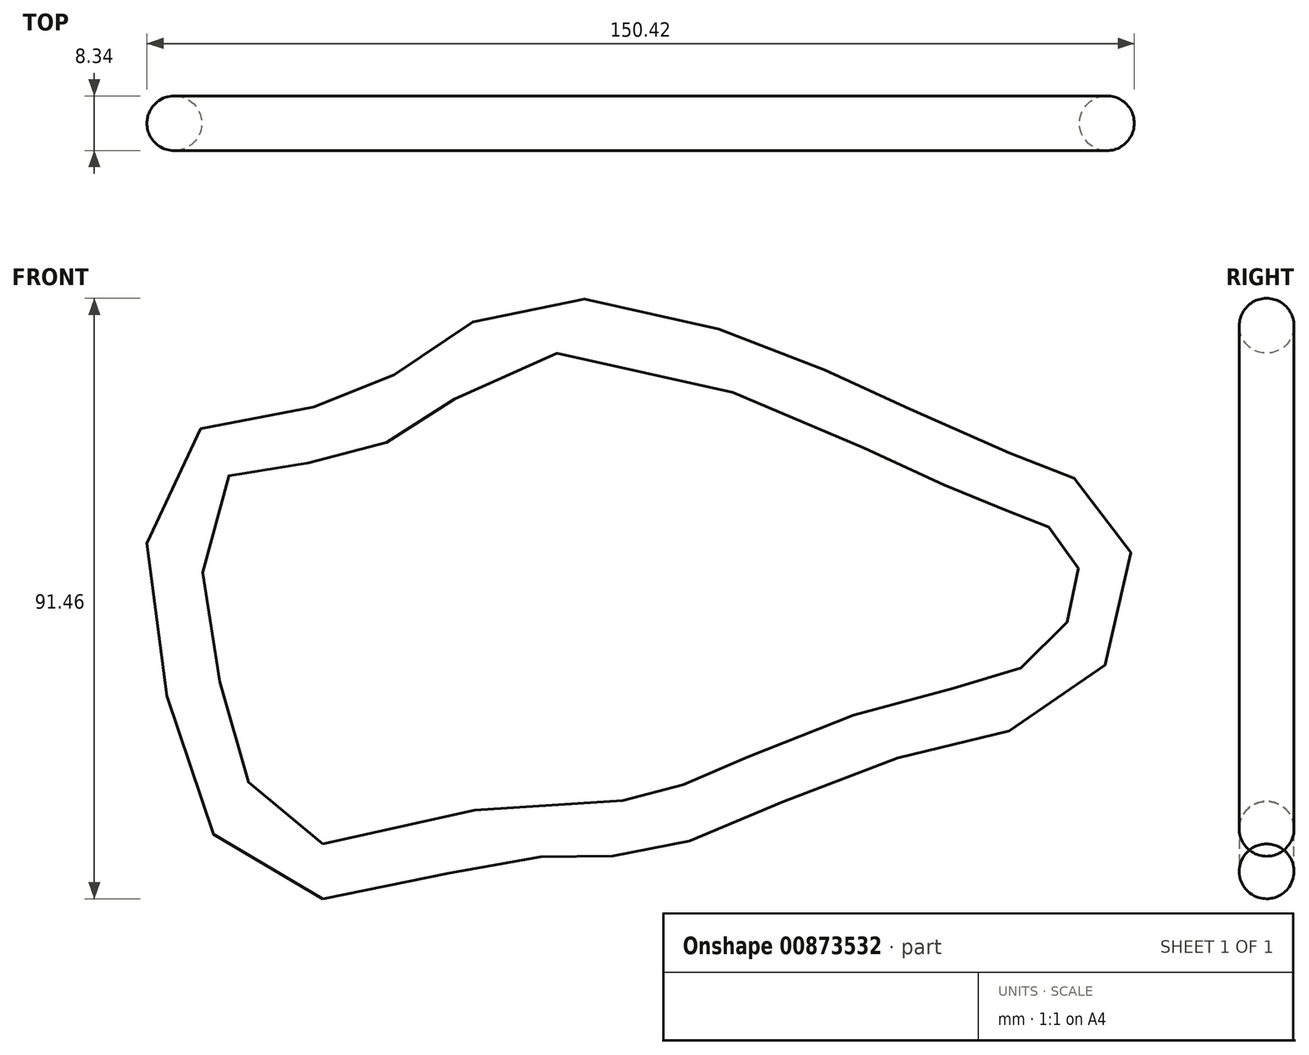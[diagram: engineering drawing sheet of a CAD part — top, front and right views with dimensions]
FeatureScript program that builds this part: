
annotation { "Feature Type Name" : "Feature", "Feature Type Description" : "" }
export const myFeature = defineFeature(function(context is Context, id is Id, definition is map)
    precondition{}
    {
        {
            var Q0;
            Q0=qCreatedBy(makeId("Front.planeOp"),FACE);
            var sketch = newSketch(context, id + "F0", { "sketchPlane" : qUnion([Q0])});
            skFitSpline(sketch, "E0", {"points": [v(58.3, 31.4) * mm, v(37.13, 40.64) * mm, v(20.45, 48) * mm, v(-11.8, 55.9) * mm, v(-28.83, 49.23) * mm, v(-45.61, 39.95) * mm, v(-67.02, 34.86) * mm, v(-67.92, 1.57) * mm, v(-53.89, -26.2) * mm, v(-26.04, -22.44) * mm, v(-10, -20.69) * mm, v(0, -20.36) * mm, v(12.13, -16.37) * mm, v(40.6, -5.33) * mm, v(63.6, 2.16) * mm, v(71.35, 19.03) * mm, v(64.93, 28.73) * mm, v(58.3, 31.4) * mm]});
            skLineSegment(sketch, "E1", {"start": v(-64.2, -27.2) * mm, "end": v(-42.5, -27.2) * mm, "construction": true});
            skPoint(sketch, "E2", {"position": v(-48.03, -27.2) * mm});
            skSolve(sketch);
        }
        {
            var Q0;
            Q0=sQuery(id+"F0.wireOp",VERTEX,"E2");
            var Q1;
            Q1=sQuery(id+"F0.wireOp",EDGE,"E0");
            cPlane(context, id + "F1", {"entities" : qUnion([Q0, Q1]), "cplaneType" : CPlaneType.CURVE_POINT, "offset" : 25.4 * mm, "width" : 152.4 * mm, "height" : 152.4 * mm});
        }
        {
            var Q0;
            Q0=qCreatedBy(id+"F1.planeOp",FACE);
            var sketch = newSketch(context, id + "F2", { "sketchPlane" : qUnion([Q0])});
            skCircle(sketch, "E3", {"center": v(0, -27.2) * mm, "radius": 4.17 * mm});
            skSolve(sketch);
        }
        {
            var Q0;
            Q0=makeQuery(id+"F2.imprint","IMPRINT",FACE,{"disambiguationData":[TD([[makeQuery(id+"F2.imprint","IMPRINT",EDGE,{"derivedFrom":sQuery(id+"F2.wireOp",EDGE,"E3")}),1.0]])]});
            var Q1;
            Q1=sQuery(id+"F0.wireOp",EDGE,"E0");
            sweep(context, id + "F3", {"profiles" : qUnion([Q0]), "path" : qUnion([Q1])});
        }
    });
